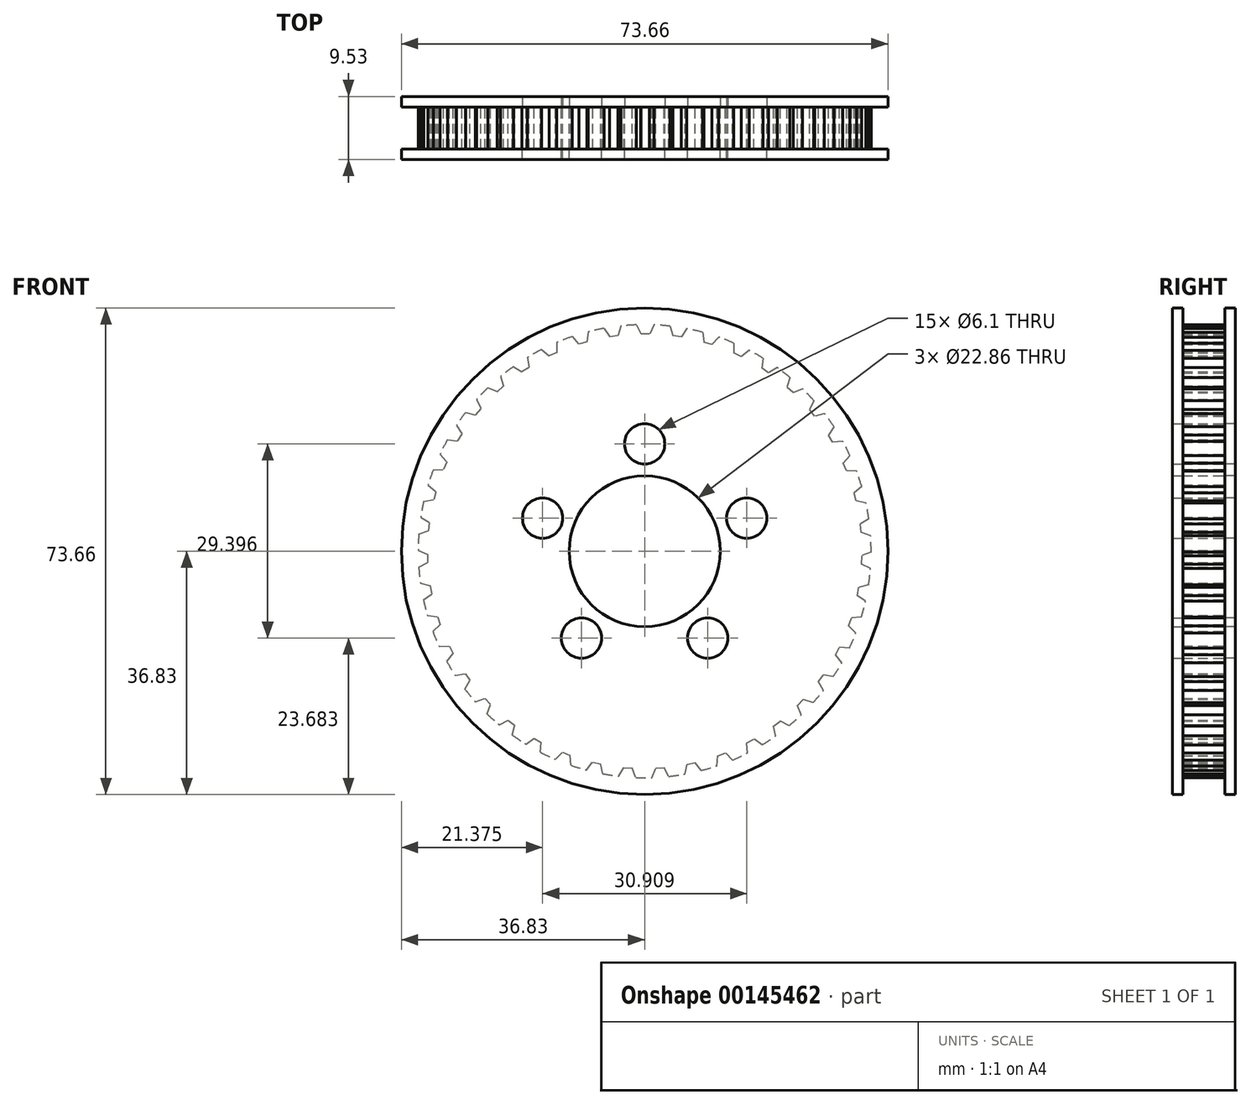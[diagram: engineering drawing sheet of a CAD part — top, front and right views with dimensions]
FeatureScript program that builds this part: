
annotation { "Feature Type Name" : "Feature", "Feature Type Description" : "" }
export const myFeature = defineFeature(function(context is Context, id is Id, definition is map)
    precondition{}
    {
        {
            var Q0;
            Q0=qCreatedBy(makeId("Front.planeOp"),FACE);
            var sketch = newSketch(context, id + "F0", { "sketchPlane" : qUnion([Q0])});
            skCircle(sketch, "E0", {"center": v(0, 0) * mm, "radius": 34.3 * mm});
            skLineSegment(sketch, "E1", {"start": v(-1.27, 34.27) * mm, "end": v(-0.64, 33) * mm});
            skLineSegment(sketch, "E2", {"start": v(-0.64, 33) * mm, "end": v(0, 33) * mm});
            skLineSegment(sketch, "E3.MirrorCS", {"start": v(0.64, 33) * mm, "end": v(0, 33) * mm});
            skLineSegment(sketch, "E4.MirrorCS", {"start": v(1.27, 34.27) * mm, "end": v(0.64, 33) * mm});
            skPoint(sketch, "E5", {"position": v(5.11, 33.9) * mm});
            skLineSegment(sketch, "E6", {"start": v(5.11, 33.9) * mm, "end": v(0, 0) * mm, "construction": true});
            skLineSegment(sketch, "E7", {"start": v(3.85, 34.07) * mm, "end": v(4.27, 32.61) * mm});
            skLineSegment(sketch, "E8", {"start": v(4.27, 32.61) * mm, "end": v(4.9, 32.52) * mm});
            skLineSegment(sketch, "E9.MirrorCS", {"start": v(5.53, 32.42) * mm, "end": v(4.9, 32.52) * mm});
            skLineSegment(sketch, "E10.MirrorCS", {"start": v(6.36, 33.7) * mm, "end": v(5.53, 32.42) * mm});
            skLineSegment(sketch, "E11.1.0", {"start": v(-31.43, -13.7) * mm, "end": v(-30.38, -12.6) * mm});
            skLineSegment(sketch, "E11.1.1", {"start": v(-32.36, -11.34) * mm, "end": v(-30.85, -11.42) * mm});
            skLineSegment(sketch, "E11.2.0", {"start": v(27.58, -20.37) * mm, "end": v(26.1, -20) * mm});
            skLineSegment(sketch, "E11.2.1", {"start": v(26, -22.36) * mm, "end": v(25.32, -21) * mm});
            skLineSegment(sketch, "E12.1.0", {"start": v(-0.52, 32.89) * mm, "end": v(0.11, 32.89) * mm});
            skLineSegment(sketch, "E12.1.1", {"start": v(0.75, 32.88) * mm, "end": v(0.11, 32.89) * mm});
            skLineSegment(sketch, "E12.1.2", {"start": v(-1.15, 34.27) * mm, "end": v(-0.52, 32.89) * mm});
            skLineSegment(sketch, "E12.1.3", {"start": v(1.39, 34.26) * mm, "end": v(0.75, 32.88) * mm});
            skLineSegment(sketch, "E12.2.0", {"start": v(-5.3, 32.46) * mm, "end": v(-4.68, 32.55) * mm});
            skLineSegment(sketch, "E12.2.1", {"start": v(-4.05, 32.64) * mm, "end": v(-4.68, 32.55) * mm});
            skLineSegment(sketch, "E12.2.2", {"start": v(-6.13, 33.74) * mm, "end": v(-5.3, 32.46) * mm});
            skLineSegment(sketch, "E12.2.3", {"start": v(-3.61, 34.1) * mm, "end": v(-4.05, 32.64) * mm});
            skLineSegment(sketch, "E12.3.0", {"start": v(-9.97, 31.34) * mm, "end": v(-9.36, 31.52) * mm});
            skLineSegment(sketch, "E12.3.1", {"start": v(-8.76, 31.7) * mm, "end": v(-9.36, 31.52) * mm});
            skLineSegment(sketch, "E12.3.2", {"start": v(-10.98, 32.49) * mm, "end": v(-9.97, 31.34) * mm});
            skLineSegment(sketch, "E12.3.3", {"start": v(-8.54, 33.2) * mm, "end": v(-8.76, 31.7) * mm});
            skLineSegment(sketch, "E12.4.0", {"start": v(-14.43, 29.56) * mm, "end": v(-13.86, 29.83) * mm});
            skLineSegment(sketch, "E12.4.1", {"start": v(-13.28, 30.1) * mm, "end": v(-13.86, 29.83) * mm});
            skLineSegment(sketch, "E12.4.2", {"start": v(-15.59, 30.54) * mm, "end": v(-14.43, 29.56) * mm});
            skLineSegment(sketch, "E12.4.3", {"start": v(-13.29, 31.61) * mm, "end": v(-13.28, 30.1) * mm});
            skLineSegment(sketch, "E12.5.0", {"start": v(-18.58, 27.14) * mm, "end": v(-18.05, 27.5) * mm});
            skLineSegment(sketch, "E12.5.1", {"start": v(-17.52, 27.84) * mm, "end": v(-18.05, 27.5) * mm});
            skLineSegment(sketch, "E12.5.2", {"start": v(-19.87, 27.95) * mm, "end": v(-18.58, 27.14) * mm});
            skLineSegment(sketch, "E12.5.3", {"start": v(-17.75, 29.34) * mm, "end": v(-17.52, 27.84) * mm});
            skLineSegment(sketch, "E12.6.0", {"start": v(-22.33, 24.15) * mm, "end": v(-21.86, 24.57) * mm});
            skLineSegment(sketch, "E12.6.1", {"start": v(-21.39, 25) * mm, "end": v(-21.86, 24.57) * mm});
            skLineSegment(sketch, "E12.6.2", {"start": v(-23.73, 24.76) * mm, "end": v(-22.33, 24.15) * mm});
            skLineSegment(sketch, "E12.6.3", {"start": v(-21.83, 26.44) * mm, "end": v(-21.39, 25) * mm});
            skLineSegment(sketch, "E12.7.0", {"start": v(-25.61, 20.64) * mm, "end": v(-25.2, 21.12) * mm});
            skLineSegment(sketch, "E12.7.1", {"start": v(-24.8, 21.61) * mm, "end": v(-25.2, 21.12) * mm});
            skLineSegment(sketch, "E12.7.2", {"start": v(-27.08, 21.04) * mm, "end": v(-25.61, 20.64) * mm});
            skLineSegment(sketch, "E12.7.3", {"start": v(-25.45, 22.98) * mm, "end": v(-24.8, 21.61) * mm});
            skLineSegment(sketch, "E12.8.0", {"start": v(-28.34, 16.69) * mm, "end": v(-28.01, 17.23) * mm});
            skLineSegment(sketch, "E12.8.1", {"start": v(-27.68, 17.77) * mm, "end": v(-28.01, 17.23) * mm});
            skLineSegment(sketch, "E12.8.2", {"start": v(-29.85, 16.87) * mm, "end": v(-28.34, 16.69) * mm});
            skLineSegment(sketch, "E12.8.3", {"start": v(-28.52, 19.03) * mm, "end": v(-27.68, 17.77) * mm});
            skLineSegment(sketch, "E12.9.0", {"start": v(-30.47, 12.38) * mm, "end": v(-30.22, 12.97) * mm});
            skLineSegment(sketch, "E12.9.1", {"start": v(-29.97, 13.55) * mm, "end": v(-30.22, 12.97) * mm});
            skLineSegment(sketch, "E12.9.2", {"start": v(-32, 12.34) * mm, "end": v(-30.47, 12.38) * mm});
            skLineSegment(sketch, "E12.9.3", {"start": v(-30.99, 14.68) * mm, "end": v(-29.97, 13.55) * mm});
            skLineSegment(sketch, "E12.10.0", {"start": v(-31.95, 7.81) * mm, "end": v(-31.79, 8.43) * mm});
            skLineSegment(sketch, "E12.10.1", {"start": v(-31.63, 9.04) * mm, "end": v(-31.79, 8.43) * mm});
            skLineSegment(sketch, "E12.10.2", {"start": v(-33.45, 7.56) * mm, "end": v(-31.95, 7.81) * mm});
            skLineSegment(sketch, "E12.10.3", {"start": v(-32.8, 10) * mm, "end": v(-31.63, 9.04) * mm});
            skLineSegment(sketch, "E12.11.0", {"start": v(-32.75, 3.08) * mm, "end": v(-32.68, 3.71) * mm});
            skLineSegment(sketch, "E12.11.1", {"start": v(-32.6, 4.34) * mm, "end": v(-32.68, 3.71) * mm});
            skLineSegment(sketch, "E12.11.2", {"start": v(-34.2, 2.6) * mm, "end": v(-32.75, 3.08) * mm});
            skLineSegment(sketch, "E12.11.3", {"start": v(-33.9, 5.13) * mm, "end": v(-32.6, 4.34) * mm});
            skLineSegment(sketch, "E12.12.0", {"start": v(-32.85, -1.72) * mm, "end": v(-32.87, -1.09) * mm});
            skLineSegment(sketch, "E12.12.1", {"start": v(-32.89, -0.45) * mm, "end": v(-32.87, -1.09) * mm});
            skLineSegment(sketch, "E12.12.2", {"start": v(-34.2, -2.4) * mm, "end": v(-32.85, -1.72) * mm});
            skLineSegment(sketch, "E12.12.3", {"start": v(-34.29, 0.14) * mm, "end": v(-32.89, -0.45) * mm});
            skLineSegment(sketch, "E12.13.0", {"start": v(-32.25, -6.49) * mm, "end": v(-32.36, -5.86) * mm});
            skLineSegment(sketch, "E12.13.1", {"start": v(-32.47, -5.24) * mm, "end": v(-32.36, -5.86) * mm});
            skLineSegment(sketch, "E12.13.2", {"start": v(-33.5, -7.36) * mm, "end": v(-32.25, -6.49) * mm});
            skLineSegment(sketch, "E12.13.3", {"start": v(-33.94, -4.86) * mm, "end": v(-32.47, -5.24) * mm});
            skLineSegment(sketch, "E12.14.0", {"start": v(-30.96, -11.11) * mm, "end": v(-31.16, -10.51) * mm});
            skLineSegment(sketch, "E12.14.1", {"start": v(-31.36, -9.9) * mm, "end": v(-31.16, -10.51) * mm});
            skLineSegment(sketch, "E12.14.2", {"start": v(-32.06, -12.15) * mm, "end": v(-30.96, -11.11) * mm});
            skLineSegment(sketch, "E12.14.3", {"start": v(-32.88, -9.75) * mm, "end": v(-31.36, -9.9) * mm});
            skLineSegment(sketch, "E12.15.0", {"start": v(-29.01, -15.5) * mm, "end": v(-29.3, -14.94) * mm});
            skLineSegment(sketch, "E12.15.1", {"start": v(-29.59, -14.37) * mm, "end": v(-29.3, -14.94) * mm});
            skLineSegment(sketch, "E12.15.2", {"start": v(-29.95, -16.7) * mm, "end": v(-29.01, -15.5) * mm});
            skLineSegment(sketch, "E12.15.3", {"start": v(-31.1, -14.43) * mm, "end": v(-29.59, -14.37) * mm});
            skLineSegment(sketch, "E12.16.0", {"start": v(-26.44, -19.56) * mm, "end": v(-26.81, -19.04) * mm});
            skLineSegment(sketch, "E12.16.1", {"start": v(-27.18, -18.52) * mm, "end": v(-26.81, -19.04) * mm});
            skLineSegment(sketch, "E12.16.2", {"start": v(-27.2, -20.88) * mm, "end": v(-26.44, -19.56) * mm});
            skLineSegment(sketch, "E12.16.3", {"start": v(-28.67, -18.8) * mm, "end": v(-27.18, -18.52) * mm});
            skLineSegment(sketch, "E12.17.0", {"start": v(-23.32, -23.2) * mm, "end": v(-23.75, -22.74) * mm});
            skLineSegment(sketch, "E12.17.1", {"start": v(-24.2, -22.28) * mm, "end": v(-23.75, -22.74) * mm});
            skLineSegment(sketch, "E12.17.2", {"start": v(-23.87, -24.61) * mm, "end": v(-23.32, -23.2) * mm});
            skLineSegment(sketch, "E12.17.3", {"start": v(-25.63, -22.78) * mm, "end": v(-24.2, -22.28) * mm});
            skLineSegment(sketch, "E12.18.0", {"start": v(-19.69, -26.35) * mm, "end": v(-20.19, -25.96) * mm});
            skLineSegment(sketch, "E12.18.1", {"start": v(-20.7, -25.57) * mm, "end": v(-20.19, -25.96) * mm});
            skLineSegment(sketch, "E12.18.2", {"start": v(-20.03, -27.83) * mm, "end": v(-19.69, -26.35) * mm});
            skLineSegment(sketch, "E12.18.3", {"start": v(-22.04, -26.27) * mm, "end": v(-20.7, -25.57) * mm});
            skLineSegment(sketch, "E12.19.0", {"start": v(-15.64, -28.94) * mm, "end": v(-16.2, -28.62) * mm});
            skLineSegment(sketch, "E12.19.1", {"start": v(-16.75, -28.3) * mm, "end": v(-16.2, -28.62) * mm});
            skLineSegment(sketch, "E12.19.2", {"start": v(-15.77, -30.45) * mm, "end": v(-15.64, -28.94) * mm});
            skLineSegment(sketch, "E12.19.3", {"start": v(-17.98, -29.2) * mm, "end": v(-16.75, -28.3) * mm});
            skLineSegment(sketch, "E12.20.0", {"start": v(-11.26, -30.9) * mm, "end": v(-11.85, -30.68) * mm});
            skLineSegment(sketch, "E12.20.1", {"start": v(-12.45, -30.45) * mm, "end": v(-11.85, -30.68) * mm});
            skLineSegment(sketch, "E12.20.2", {"start": v(-11.17, -32.42) * mm, "end": v(-11.26, -30.9) * mm});
            skLineSegment(sketch, "E12.20.3", {"start": v(-13.54, -31.5) * mm, "end": v(-12.45, -30.45) * mm});
            skLineSegment(sketch, "E12.21.0", {"start": v(-6.64, -32.21) * mm, "end": v(-7.26, -32.07) * mm});
            skLineSegment(sketch, "E12.21.1", {"start": v(-7.88, -31.93) * mm, "end": v(-7.26, -32.07) * mm});
            skLineSegment(sketch, "E12.21.2", {"start": v(-6.33, -33.7) * mm, "end": v(-6.64, -32.21) * mm});
            skLineSegment(sketch, "E12.21.3", {"start": v(-8.8, -33.14) * mm, "end": v(-7.88, -31.93) * mm});
            skLineSegment(sketch, "E12.22.0", {"start": v(-1.88, -32.84) * mm, "end": v(-2.51, -32.8) * mm});
            skLineSegment(sketch, "E12.22.1", {"start": v(-3.15, -32.74) * mm, "end": v(-2.51, -32.8) * mm});
            skLineSegment(sketch, "E12.22.2", {"start": v(-1.35, -34.26) * mm, "end": v(-1.88, -32.84) * mm});
            skLineSegment(sketch, "E12.22.3", {"start": v(-3.89, -34.07) * mm, "end": v(-3.15, -32.74) * mm});
            skLineSegment(sketch, "E12.23.0", {"start": v(2.92, -32.76) * mm, "end": v(2.29, -32.8) * mm});
            skLineSegment(sketch, "E12.23.1", {"start": v(1.65, -32.85) * mm, "end": v(2.29, -32.8) * mm});
            skLineSegment(sketch, "E12.23.2", {"start": v(3.65, -34.1) * mm, "end": v(2.92, -32.76) * mm});
            skLineSegment(sketch, "E12.23.3", {"start": v(1.12, -34.27) * mm, "end": v(1.65, -32.85) * mm});
            skLineSegment(sketch, "E12.24.0", {"start": v(7.66, -31.99) * mm, "end": v(7.04, -32.12) * mm});
            skLineSegment(sketch, "E12.24.1", {"start": v(6.42, -32.26) * mm, "end": v(7.04, -32.12) * mm});
            skLineSegment(sketch, "E12.24.2", {"start": v(8.57, -33.2) * mm, "end": v(7.66, -31.99) * mm});
            skLineSegment(sketch, "E12.24.3", {"start": v(6.1, -33.74) * mm, "end": v(6.42, -32.26) * mm});
            skLineSegment(sketch, "E12.25.0", {"start": v(12.24, -30.53) * mm, "end": v(11.64, -30.76) * mm});
            skLineSegment(sketch, "E12.25.1", {"start": v(11.05, -30.98) * mm, "end": v(11.64, -30.76) * mm});
            skLineSegment(sketch, "E12.25.2", {"start": v(13.32, -31.6) * mm, "end": v(12.24, -30.53) * mm});
            skLineSegment(sketch, "E12.25.3", {"start": v(10.94, -32.5) * mm, "end": v(11.05, -30.98) * mm});
            skLineSegment(sketch, "E12.26.0", {"start": v(16.55, -28.43) * mm, "end": v(16, -28.73) * mm});
            skLineSegment(sketch, "E12.26.1", {"start": v(15.44, -29.04) * mm, "end": v(16, -28.73) * mm});
            skLineSegment(sketch, "E12.26.2", {"start": v(17.78, -29.32) * mm, "end": v(16.55, -28.43) * mm});
            skLineSegment(sketch, "E12.26.3", {"start": v(15.56, -30.56) * mm, "end": v(15.44, -29.04) * mm});
            skLineSegment(sketch, "E12.27.0", {"start": v(20.51, -25.71) * mm, "end": v(20, -26.1) * mm});
            skLineSegment(sketch, "E12.27.1", {"start": v(19.5, -26.49) * mm, "end": v(20, -26.1) * mm});
            skLineSegment(sketch, "E12.27.2", {"start": v(21.86, -26.42) * mm, "end": v(20.51, -25.71) * mm});
            skLineSegment(sketch, "E12.27.3", {"start": v(19.84, -27.97) * mm, "end": v(19.5, -26.49) * mm});
            skLineSegment(sketch, "E12.28.0", {"start": v(24.04, -22.45) * mm, "end": v(23.6, -22.9) * mm});
            skLineSegment(sketch, "E12.28.1", {"start": v(23.15, -23.36) * mm, "end": v(23.6, -22.9) * mm});
            skLineSegment(sketch, "E12.28.2", {"start": v(25.47, -22.96) * mm, "end": v(24.04, -22.45) * mm});
            skLineSegment(sketch, "E12.28.3", {"start": v(23.7, -24.78) * mm, "end": v(23.15, -23.36) * mm});
            skLineSegment(sketch, "E12.29.0", {"start": v(27.05, -18.71) * mm, "end": v(26.68, -19.23) * mm});
            skLineSegment(sketch, "E12.29.1", {"start": v(26.3, -19.74) * mm, "end": v(26.68, -19.23) * mm});
            skLineSegment(sketch, "E12.29.2", {"start": v(28.54, -19) * mm, "end": v(27.05, -18.71) * mm});
            skLineSegment(sketch, "E12.29.3", {"start": v(27.06, -21.07) * mm, "end": v(26.3, -19.74) * mm});
            skLineSegment(sketch, "E12.30.0", {"start": v(29.49, -14.58) * mm, "end": v(29.2, -15.14) * mm});
            skLineSegment(sketch, "E12.30.1", {"start": v(28.9, -15.7) * mm, "end": v(29.2, -15.14) * mm});
            skLineSegment(sketch, "E12.30.2", {"start": v(31, -14.65) * mm, "end": v(29.49, -14.58) * mm});
            skLineSegment(sketch, "E12.30.3", {"start": v(29.84, -16.9) * mm, "end": v(28.9, -15.7) * mm});
            skLineSegment(sketch, "E12.31.0", {"start": v(31.3, -10.13) * mm, "end": v(31.09, -10.73) * mm});
            skLineSegment(sketch, "E12.31.1", {"start": v(30.88, -11.33) * mm, "end": v(31.09, -10.73) * mm});
            skLineSegment(sketch, "E12.31.2", {"start": v(32.8, -9.98) * mm, "end": v(31.3, -10.13) * mm});
            skLineSegment(sketch, "E12.31.3", {"start": v(31.98, -12.38) * mm, "end": v(30.88, -11.33) * mm});
            skLineSegment(sketch, "E12.32.0", {"start": v(32.44, -5.46) * mm, "end": v(32.32, -6.09) * mm});
            skLineSegment(sketch, "E12.32.1", {"start": v(32.2, -6.7) * mm, "end": v(32.32, -6.09) * mm});
            skLineSegment(sketch, "E12.32.2", {"start": v(33.9, -5.1) * mm, "end": v(32.44, -5.46) * mm});
            skLineSegment(sketch, "E12.32.3", {"start": v(33.44, -7.59) * mm, "end": v(32.2, -6.7) * mm});
            skLineSegment(sketch, "E12.33.0", {"start": v(32.89, -0.68) * mm, "end": v(32.86, -1.32) * mm});
            skLineSegment(sketch, "E12.33.1", {"start": v(32.83, -1.95) * mm, "end": v(32.86, -1.32) * mm});
            skLineSegment(sketch, "E12.33.2", {"start": v(34.29, -0.1) * mm, "end": v(32.89, -0.68) * mm});
            skLineSegment(sketch, "E12.33.3", {"start": v(34.19, -2.64) * mm, "end": v(32.83, -1.95) * mm});
            skLineSegment(sketch, "E12.34.0", {"start": v(32.63, 4.11) * mm, "end": v(32.7, 3.48) * mm});
            skLineSegment(sketch, "E12.34.1", {"start": v(32.77, 2.85) * mm, "end": v(32.7, 3.48) * mm});
            skLineSegment(sketch, "E12.34.2", {"start": v(33.94, 4.9) * mm, "end": v(32.63, 4.11) * mm});
            skLineSegment(sketch, "E12.34.3", {"start": v(34.2, 2.37) * mm, "end": v(32.77, 2.85) * mm});
            skLineSegment(sketch, "E12.35.0", {"start": v(31.69, 8.82) * mm, "end": v(31.85, 8.2) * mm});
            skLineSegment(sketch, "E12.35.1", {"start": v(32, 7.6) * mm, "end": v(31.85, 8.2) * mm});
            skLineSegment(sketch, "E12.35.2", {"start": v(32.87, 9.78) * mm, "end": v(31.69, 8.82) * mm});
            skLineSegment(sketch, "E12.35.3", {"start": v(33.5, 7.32) * mm, "end": v(32, 7.6) * mm});
            skLineSegment(sketch, "E12.36.0", {"start": v(30.07, 13.34) * mm, "end": v(30.31, 12.76) * mm});
            skLineSegment(sketch, "E12.36.1", {"start": v(30.56, 12.17) * mm, "end": v(30.31, 12.76) * mm});
            skLineSegment(sketch, "E12.36.2", {"start": v(31.1, 14.46) * mm, "end": v(30.07, 13.34) * mm});
            skLineSegment(sketch, "E12.36.3", {"start": v(32.08, 12.12) * mm, "end": v(30.56, 12.17) * mm});
            skLineSegment(sketch, "E12.37.0", {"start": v(27.8, 17.58) * mm, "end": v(28.13, 17.03) * mm});
            skLineSegment(sketch, "E12.37.1", {"start": v(28.46, 16.5) * mm, "end": v(28.13, 17.03) * mm});
            skLineSegment(sketch, "E12.37.2", {"start": v(28.65, 18.84) * mm, "end": v(27.8, 17.58) * mm});
            skLineSegment(sketch, "E12.37.3", {"start": v(29.97, 16.66) * mm, "end": v(28.46, 16.5) * mm});
            skLineSegment(sketch, "E12.38.0", {"start": v(24.95, 21.44) * mm, "end": v(25.35, 20.95) * mm});
            skLineSegment(sketch, "E12.38.1", {"start": v(25.76, 20.46) * mm, "end": v(25.35, 20.95) * mm});
            skLineSegment(sketch, "E12.38.2", {"start": v(25.6, 22.8) * mm, "end": v(24.95, 21.44) * mm});
            skLineSegment(sketch, "E12.38.3", {"start": v(27.22, 20.85) * mm, "end": v(25.76, 20.46) * mm});
            skLineSegment(sketch, "E12.39.0", {"start": v(21.56, 24.84) * mm, "end": v(22.03, 24.42) * mm});
            skLineSegment(sketch, "E12.39.1", {"start": v(22.5, 24) * mm, "end": v(22.03, 24.42) * mm});
            skLineSegment(sketch, "E12.39.2", {"start": v(22.01, 26.3) * mm, "end": v(21.56, 24.84) * mm});
            skLineSegment(sketch, "E12.39.3", {"start": v(23.9, 24.6) * mm, "end": v(22.5, 24) * mm});
            skCircle(sketch, "E13", {"center": v(0, 16.25) * mm, "radius": 3.05 * mm});
            skCircle(sketch, "E14.1.0", {"center": v(-15.45, 5.02) * mm, "radius": 3.05 * mm});
            skCircle(sketch, "E14.2.0", {"center": v(-9.55, -13.15) * mm, "radius": 3.05 * mm});
            skCircle(sketch, "E14.3.0", {"center": v(9.55, -13.15) * mm, "radius": 3.05 * mm});
            skCircle(sketch, "E14.4.0", {"center": v(15.45, 5.02) * mm, "radius": 3.05 * mm});
            skLineSegment(sketch, "E15.1.40.0", {"start": v(17.71, 27.72) * mm, "end": v(18.24, 27.36) * mm});
            skLineSegment(sketch, "E15.3.40.0", {"start": v(18.77, 27.01) * mm, "end": v(18.24, 27.36) * mm});
            skLineSegment(sketch, "E15.6.40.0", {"start": v(17.95, 29.22) * mm, "end": v(17.71, 27.72) * mm});
            skLineSegment(sketch, "E15.9.40.0", {"start": v(20.06, 27.8) * mm, "end": v(18.77, 27.01) * mm});
            skLineSegment(sketch, "E16.1.41.0", {"start": v(13.49, 30) * mm, "end": v(14.06, 29.73) * mm});
            skLineSegment(sketch, "E16.3.41.0", {"start": v(14.64, 29.46) * mm, "end": v(14.06, 29.73) * mm});
            skLineSegment(sketch, "E16.6.41.0", {"start": v(13.5, 31.52) * mm, "end": v(13.49, 30) * mm});
            skLineSegment(sketch, "E16.9.41.0", {"start": v(15.8, 30.43) * mm, "end": v(14.64, 29.46) * mm});
            skLineSegment(sketch, "E17.1.42.0", {"start": v(8.98, 31.64) * mm, "end": v(9.58, 31.46) * mm});
            skLineSegment(sketch, "E17.3.42.0", {"start": v(10.2, 31.27) * mm, "end": v(9.58, 31.46) * mm});
            skLineSegment(sketch, "E17.6.42.0", {"start": v(8.77, 33.15) * mm, "end": v(8.98, 31.64) * mm});
            skLineSegment(sketch, "E17.9.42.0", {"start": v(11.2, 32.4) * mm, "end": v(10.2, 31.27) * mm});
            skCircle(sketch, "E18", {"center": v(0, 0) * mm, "radius": 11.43 * mm});
            skLineSegment(sketch, "E19", {"start": v(-8.54, 33.2) * mm, "end": v(-6.13, 33.74) * mm, "construction": true});
            skSolve(sketch);
        }
        {
            var Q0;
            {var subQ60=sQuery(id+"F0.wireOp",EDGE,"E7");Q0=makeQuery(id+"F0.imprint","IMPRINT",FACE,{"disambiguationData":[TD([[makeQuery(id+"F0.imprint","IMPRINT",EDGE,{"derivedFrom":subQ60}),-1.0]])]});}
            extrude(context, id + "F1", {"entities" : qUnion([Q0]), "depth" : 6.35 * mm});
        }
        {
            var Q0;
            Q0=makeQuery(id+"F1.opExtrude","CAP_FACE",FACE,{"disambiguationData":[OSD([sQuery(id+"F0.wireOp",EDGE,"E0"),sQuery(id+"F0.wireOp",EDGE,"E1"),sQuery(id+"F0.wireOp",EDGE,"E4.MirrorCS"),sQuery(id+"F0.wireOp",EDGE,"E7"),sQuery(id+"F0.wireOp",EDGE,"E8"),sQuery(id+"F0.wireOp",EDGE,"E9.MirrorCS"),sQuery(id+"F0.wireOp",EDGE,"E10.MirrorCS"),sQuery(id+"F0.wireOp",EDGE,"E12.1.0"),sQuery(id+"F0.wireOp",EDGE,"E12.1.1"),sQuery(id+"F0.wireOp",EDGE,"E12.1.2"),sQuery(id+"F0.wireOp",EDGE,"E12.1.3"),sQuery(id+"F0.wireOp",EDGE,"E12.2.0"),sQuery(id+"F0.wireOp",EDGE,"E12.2.1"),sQuery(id+"F0.wireOp",EDGE,"E12.2.2"),sQuery(id+"F0.wireOp",EDGE,"E12.2.3"),sQuery(id+"F0.wireOp",EDGE,"E12.3.0"),sQuery(id+"F0.wireOp",EDGE,"E12.3.1"),sQuery(id+"F0.wireOp",EDGE,"E12.3.2"),sQuery(id+"F0.wireOp",EDGE,"E12.3.3"),sQuery(id+"F0.wireOp",EDGE,"E12.4.0"),sQuery(id+"F0.wireOp",EDGE,"E12.4.1"),sQuery(id+"F0.wireOp",EDGE,"E12.4.2"),sQuery(id+"F0.wireOp",EDGE,"E12.4.3"),sQuery(id+"F0.wireOp",EDGE,"E12.5.0"),sQuery(id+"F0.wireOp",EDGE,"E12.5.1"),sQuery(id+"F0.wireOp",EDGE,"E12.5.2"),sQuery(id+"F0.wireOp",EDGE,"E12.5.3"),sQuery(id+"F0.wireOp",EDGE,"E12.6.0"),sQuery(id+"F0.wireOp",EDGE,"E12.6.1"),sQuery(id+"F0.wireOp",EDGE,"E12.6.2"),sQuery(id+"F0.wireOp",EDGE,"E12.6.3"),sQuery(id+"F0.wireOp",EDGE,"E12.7.0"),sQuery(id+"F0.wireOp",EDGE,"E12.7.1"),sQuery(id+"F0.wireOp",EDGE,"E12.7.2"),sQuery(id+"F0.wireOp",EDGE,"E12.7.3"),sQuery(id+"F0.wireOp",EDGE,"E12.8.0"),sQuery(id+"F0.wireOp",EDGE,"E12.8.1"),sQuery(id+"F0.wireOp",EDGE,"E12.8.2"),sQuery(id+"F0.wireOp",EDGE,"E12.8.3"),sQuery(id+"F0.wireOp",EDGE,"E12.9.0"),sQuery(id+"F0.wireOp",EDGE,"E12.9.1"),sQuery(id+"F0.wireOp",EDGE,"E12.9.2"),sQuery(id+"F0.wireOp",EDGE,"E12.9.3"),sQuery(id+"F0.wireOp",EDGE,"E12.10.0"),sQuery(id+"F0.wireOp",EDGE,"E12.10.1"),sQuery(id+"F0.wireOp",EDGE,"E12.10.2"),sQuery(id+"F0.wireOp",EDGE,"E12.10.3"),sQuery(id+"F0.wireOp",EDGE,"E12.11.0"),sQuery(id+"F0.wireOp",EDGE,"E12.11.1"),sQuery(id+"F0.wireOp",EDGE,"E12.11.2"),sQuery(id+"F0.wireOp",EDGE,"E12.11.3"),sQuery(id+"F0.wireOp",EDGE,"E12.12.0"),sQuery(id+"F0.wireOp",EDGE,"E12.12.1"),sQuery(id+"F0.wireOp",EDGE,"E12.12.2"),sQuery(id+"F0.wireOp",EDGE,"E12.12.3"),sQuery(id+"F0.wireOp",EDGE,"E12.13.0"),sQuery(id+"F0.wireOp",EDGE,"E12.13.1"),sQuery(id+"F0.wireOp",EDGE,"E12.13.2"),sQuery(id+"F0.wireOp",EDGE,"E12.13.3"),sQuery(id+"F0.wireOp",EDGE,"E12.14.0"),sQuery(id+"F0.wireOp",EDGE,"E12.14.1"),sQuery(id+"F0.wireOp",EDGE,"E12.14.2"),sQuery(id+"F0.wireOp",EDGE,"E12.14.3"),sQuery(id+"F0.wireOp",EDGE,"E12.15.0"),sQuery(id+"F0.wireOp",EDGE,"E12.15.1"),sQuery(id+"F0.wireOp",EDGE,"E12.15.2"),sQuery(id+"F0.wireOp",EDGE,"E12.15.3"),sQuery(id+"F0.wireOp",EDGE,"E12.16.0"),sQuery(id+"F0.wireOp",EDGE,"E12.16.1"),sQuery(id+"F0.wireOp",EDGE,"E12.16.2"),sQuery(id+"F0.wireOp",EDGE,"E12.16.3"),sQuery(id+"F0.wireOp",EDGE,"E12.17.0"),sQuery(id+"F0.wireOp",EDGE,"E12.17.1"),sQuery(id+"F0.wireOp",EDGE,"E12.17.2"),sQuery(id+"F0.wireOp",EDGE,"E12.17.3"),sQuery(id+"F0.wireOp",EDGE,"E12.18.0"),sQuery(id+"F0.wireOp",EDGE,"E12.18.1"),sQuery(id+"F0.wireOp",EDGE,"E12.18.2"),sQuery(id+"F0.wireOp",EDGE,"E12.18.3"),sQuery(id+"F0.wireOp",EDGE,"E12.19.0"),sQuery(id+"F0.wireOp",EDGE,"E12.19.1"),sQuery(id+"F0.wireOp",EDGE,"E12.19.2"),sQuery(id+"F0.wireOp",EDGE,"E12.19.3"),sQuery(id+"F0.wireOp",EDGE,"E12.20.0"),sQuery(id+"F0.wireOp",EDGE,"E12.20.1"),sQuery(id+"F0.wireOp",EDGE,"E12.20.2"),sQuery(id+"F0.wireOp",EDGE,"E12.20.3"),sQuery(id+"F0.wireOp",EDGE,"E12.21.0"),sQuery(id+"F0.wireOp",EDGE,"E12.21.1"),sQuery(id+"F0.wireOp",EDGE,"E12.21.2"),sQuery(id+"F0.wireOp",EDGE,"E12.21.3"),sQuery(id+"F0.wireOp",EDGE,"E12.22.0"),sQuery(id+"F0.wireOp",EDGE,"E12.22.1"),sQuery(id+"F0.wireOp",EDGE,"E12.22.2"),sQuery(id+"F0.wireOp",EDGE,"E12.22.3"),sQuery(id+"F0.wireOp",EDGE,"E12.23.0"),sQuery(id+"F0.wireOp",EDGE,"E12.23.1"),sQuery(id+"F0.wireOp",EDGE,"E12.23.2"),sQuery(id+"F0.wireOp",EDGE,"E12.23.3"),sQuery(id+"F0.wireOp",EDGE,"E12.24.0"),sQuery(id+"F0.wireOp",EDGE,"E12.24.1"),sQuery(id+"F0.wireOp",EDGE,"E12.24.2"),sQuery(id+"F0.wireOp",EDGE,"E12.24.3"),sQuery(id+"F0.wireOp",EDGE,"E12.25.0"),sQuery(id+"F0.wireOp",EDGE,"E12.25.1"),sQuery(id+"F0.wireOp",EDGE,"E12.25.2"),sQuery(id+"F0.wireOp",EDGE,"E12.25.3"),sQuery(id+"F0.wireOp",EDGE,"E12.26.0"),sQuery(id+"F0.wireOp",EDGE,"E12.26.1"),sQuery(id+"F0.wireOp",EDGE,"E12.26.2"),sQuery(id+"F0.wireOp",EDGE,"E12.26.3"),sQuery(id+"F0.wireOp",EDGE,"E12.27.0"),sQuery(id+"F0.wireOp",EDGE,"E12.27.1"),sQuery(id+"F0.wireOp",EDGE,"E12.27.2"),sQuery(id+"F0.wireOp",EDGE,"E12.27.3"),sQuery(id+"F0.wireOp",EDGE,"E12.28.0"),sQuery(id+"F0.wireOp",EDGE,"E12.28.1"),sQuery(id+"F0.wireOp",EDGE,"E12.28.2"),sQuery(id+"F0.wireOp",EDGE,"E12.28.3"),sQuery(id+"F0.wireOp",EDGE,"E12.29.0"),sQuery(id+"F0.wireOp",EDGE,"E12.29.1"),sQuery(id+"F0.wireOp",EDGE,"E12.29.2"),sQuery(id+"F0.wireOp",EDGE,"E12.29.3"),sQuery(id+"F0.wireOp",EDGE,"E12.30.0"),sQuery(id+"F0.wireOp",EDGE,"E12.30.1"),sQuery(id+"F0.wireOp",EDGE,"E12.30.2"),sQuery(id+"F0.wireOp",EDGE,"E12.30.3"),sQuery(id+"F0.wireOp",EDGE,"E12.31.0"),sQuery(id+"F0.wireOp",EDGE,"E12.31.1"),sQuery(id+"F0.wireOp",EDGE,"E12.31.2"),sQuery(id+"F0.wireOp",EDGE,"E12.31.3"),sQuery(id+"F0.wireOp",EDGE,"E12.32.0"),sQuery(id+"F0.wireOp",EDGE,"E12.32.1"),sQuery(id+"F0.wireOp",EDGE,"E12.32.2"),sQuery(id+"F0.wireOp",EDGE,"E12.32.3"),sQuery(id+"F0.wireOp",EDGE,"E12.33.0"),sQuery(id+"F0.wireOp",EDGE,"E12.33.1"),sQuery(id+"F0.wireOp",EDGE,"E12.33.2"),sQuery(id+"F0.wireOp",EDGE,"E12.33.3"),sQuery(id+"F0.wireOp",EDGE,"E12.34.0"),sQuery(id+"F0.wireOp",EDGE,"E12.34.1"),sQuery(id+"F0.wireOp",EDGE,"E12.34.2"),sQuery(id+"F0.wireOp",EDGE,"E12.34.3"),sQuery(id+"F0.wireOp",EDGE,"E12.35.0"),sQuery(id+"F0.wireOp",EDGE,"E12.35.1"),sQuery(id+"F0.wireOp",EDGE,"E12.35.2"),sQuery(id+"F0.wireOp",EDGE,"E12.35.3"),sQuery(id+"F0.wireOp",EDGE,"E12.36.0"),sQuery(id+"F0.wireOp",EDGE,"E12.36.1"),sQuery(id+"F0.wireOp",EDGE,"E12.36.2"),sQuery(id+"F0.wireOp",EDGE,"E12.36.3"),sQuery(id+"F0.wireOp",EDGE,"E12.37.0"),sQuery(id+"F0.wireOp",EDGE,"E12.37.1"),sQuery(id+"F0.wireOp",EDGE,"E12.37.2"),sQuery(id+"F0.wireOp",EDGE,"E12.37.3"),sQuery(id+"F0.wireOp",EDGE,"E12.38.0"),sQuery(id+"F0.wireOp",EDGE,"E12.38.1"),sQuery(id+"F0.wireOp",EDGE,"E12.38.2"),sQuery(id+"F0.wireOp",EDGE,"E12.38.3"),sQuery(id+"F0.wireOp",EDGE,"E12.39.0"),sQuery(id+"F0.wireOp",EDGE,"E12.39.1"),sQuery(id+"F0.wireOp",EDGE,"E12.39.2"),sQuery(id+"F0.wireOp",EDGE,"E12.39.3"),sQuery(id+"F0.wireOp",EDGE,"E12.40.0"),sQuery(id+"F0.wireOp",EDGE,"E12.40.1"),sQuery(id+"F0.wireOp",EDGE,"E12.40.2"),sQuery(id+"F0.wireOp",EDGE,"E12.40.3"),sQuery(id+"F0.wireOp",EDGE,"E12.41.0"),sQuery(id+"F0.wireOp",EDGE,"E12.41.1"),sQuery(id+"F0.wireOp",EDGE,"E12.41.2"),sQuery(id+"F0.wireOp",EDGE,"E12.41.3"),sQuery(id+"F0.wireOp",EDGE,"E13"),sQuery(id+"F0.wireOp",EDGE,"E14.1.0"),sQuery(id+"F0.wireOp",EDGE,"E14.2.0"),sQuery(id+"F0.wireOp",EDGE,"E14.3.0"),sQuery(id+"F0.wireOp",EDGE,"E14.4.0"),sQuery(id+"F0.wireOp",EDGE,"E14.5.0"),sQuery(id+"F0.wireOp",EDGE,"E14.6.0"),sQuery(id+"F0.wireOp",EDGE,"E14.7.0"),sQuery(id+"F0.wireOp",EDGE,"E14.8.0"),sQuery(id+"F0.wireOp",EDGE,"E14.9.0")])],"isStart":false});
            var sketch = newSketch(context, id + "F2", { "sketchPlane" : qUnion([Q0])});
            skCircle(sketch, "E20", {"center": v(0, 0) * mm, "radius": 36.83 * mm});
            skCircle(sketch, "E21", {"center": v(-15.45, 5.02) * mm, "radius": 3.05 * mm});
            skCircle(sketch, "E22", {"center": v(0, 16.25) * mm, "radius": 3.05 * mm});
            skCircle(sketch, "E23", {"center": v(15.45, 5.02) * mm, "radius": 3.05 * mm});
            skCircle(sketch, "E24", {"center": v(9.55, -13.15) * mm, "radius": 3.05 * mm});
            skCircle(sketch, "E25", {"center": v(-9.55, -13.15) * mm, "radius": 3.05 * mm});
            skCircle(sketch, "E26", {"center": v(0, 0) * mm, "radius": 11.43 * mm});
            skSolve(sketch);
        }
        {
            var Q0;
            Q0 = qSketchRegion(id + "F2", true);
            extrude(context, id + "F3", {"entities" : qUnion([Q0]), "depth" : 1.59 * mm});
        }
        {
            var Q0;
            Q0=makeQuery(id+"F1.opExtrude","CAP_FACE",FACE,{"disambiguationData":[OSD([sQuery(id+"F0.wireOp",EDGE,"E0"),sQuery(id+"F0.wireOp",EDGE,"E1"),sQuery(id+"F0.wireOp",EDGE,"E4.MirrorCS"),sQuery(id+"F0.wireOp",EDGE,"E7"),sQuery(id+"F0.wireOp",EDGE,"E8"),sQuery(id+"F0.wireOp",EDGE,"E9.MirrorCS"),sQuery(id+"F0.wireOp",EDGE,"E10.MirrorCS"),sQuery(id+"F0.wireOp",EDGE,"E12.1.0"),sQuery(id+"F0.wireOp",EDGE,"E12.1.1"),sQuery(id+"F0.wireOp",EDGE,"E12.1.2"),sQuery(id+"F0.wireOp",EDGE,"E12.1.3"),sQuery(id+"F0.wireOp",EDGE,"E12.2.0"),sQuery(id+"F0.wireOp",EDGE,"E12.2.1"),sQuery(id+"F0.wireOp",EDGE,"E12.2.2"),sQuery(id+"F0.wireOp",EDGE,"E12.2.3"),sQuery(id+"F0.wireOp",EDGE,"E12.3.0"),sQuery(id+"F0.wireOp",EDGE,"E12.3.1"),sQuery(id+"F0.wireOp",EDGE,"E12.3.2"),sQuery(id+"F0.wireOp",EDGE,"E12.3.3"),sQuery(id+"F0.wireOp",EDGE,"E12.4.0"),sQuery(id+"F0.wireOp",EDGE,"E12.4.1"),sQuery(id+"F0.wireOp",EDGE,"E12.4.2"),sQuery(id+"F0.wireOp",EDGE,"E12.4.3"),sQuery(id+"F0.wireOp",EDGE,"E12.5.0"),sQuery(id+"F0.wireOp",EDGE,"E12.5.1"),sQuery(id+"F0.wireOp",EDGE,"E12.5.2"),sQuery(id+"F0.wireOp",EDGE,"E12.5.3"),sQuery(id+"F0.wireOp",EDGE,"E12.6.0"),sQuery(id+"F0.wireOp",EDGE,"E12.6.1"),sQuery(id+"F0.wireOp",EDGE,"E12.6.2"),sQuery(id+"F0.wireOp",EDGE,"E12.6.3"),sQuery(id+"F0.wireOp",EDGE,"E12.7.0"),sQuery(id+"F0.wireOp",EDGE,"E12.7.1"),sQuery(id+"F0.wireOp",EDGE,"E12.7.2"),sQuery(id+"F0.wireOp",EDGE,"E12.7.3"),sQuery(id+"F0.wireOp",EDGE,"E12.8.0"),sQuery(id+"F0.wireOp",EDGE,"E12.8.1"),sQuery(id+"F0.wireOp",EDGE,"E12.8.2"),sQuery(id+"F0.wireOp",EDGE,"E12.8.3"),sQuery(id+"F0.wireOp",EDGE,"E12.9.0"),sQuery(id+"F0.wireOp",EDGE,"E12.9.1"),sQuery(id+"F0.wireOp",EDGE,"E12.9.2"),sQuery(id+"F0.wireOp",EDGE,"E12.9.3"),sQuery(id+"F0.wireOp",EDGE,"E12.10.0"),sQuery(id+"F0.wireOp",EDGE,"E12.10.1"),sQuery(id+"F0.wireOp",EDGE,"E12.10.2"),sQuery(id+"F0.wireOp",EDGE,"E12.10.3"),sQuery(id+"F0.wireOp",EDGE,"E12.11.0"),sQuery(id+"F0.wireOp",EDGE,"E12.11.1"),sQuery(id+"F0.wireOp",EDGE,"E12.11.2"),sQuery(id+"F0.wireOp",EDGE,"E12.11.3"),sQuery(id+"F0.wireOp",EDGE,"E12.12.0"),sQuery(id+"F0.wireOp",EDGE,"E12.12.1"),sQuery(id+"F0.wireOp",EDGE,"E12.12.2"),sQuery(id+"F0.wireOp",EDGE,"E12.12.3"),sQuery(id+"F0.wireOp",EDGE,"E12.13.0"),sQuery(id+"F0.wireOp",EDGE,"E12.13.1"),sQuery(id+"F0.wireOp",EDGE,"E12.13.2"),sQuery(id+"F0.wireOp",EDGE,"E12.13.3"),sQuery(id+"F0.wireOp",EDGE,"E12.14.0"),sQuery(id+"F0.wireOp",EDGE,"E12.14.1"),sQuery(id+"F0.wireOp",EDGE,"E12.14.2"),sQuery(id+"F0.wireOp",EDGE,"E12.14.3"),sQuery(id+"F0.wireOp",EDGE,"E12.15.0"),sQuery(id+"F0.wireOp",EDGE,"E12.15.1"),sQuery(id+"F0.wireOp",EDGE,"E12.15.2"),sQuery(id+"F0.wireOp",EDGE,"E12.15.3"),sQuery(id+"F0.wireOp",EDGE,"E12.16.0"),sQuery(id+"F0.wireOp",EDGE,"E12.16.1"),sQuery(id+"F0.wireOp",EDGE,"E12.16.2"),sQuery(id+"F0.wireOp",EDGE,"E12.16.3"),sQuery(id+"F0.wireOp",EDGE,"E12.17.0"),sQuery(id+"F0.wireOp",EDGE,"E12.17.1"),sQuery(id+"F0.wireOp",EDGE,"E12.17.2"),sQuery(id+"F0.wireOp",EDGE,"E12.17.3"),sQuery(id+"F0.wireOp",EDGE,"E12.18.0"),sQuery(id+"F0.wireOp",EDGE,"E12.18.1"),sQuery(id+"F0.wireOp",EDGE,"E12.18.2"),sQuery(id+"F0.wireOp",EDGE,"E12.18.3"),sQuery(id+"F0.wireOp",EDGE,"E12.19.0"),sQuery(id+"F0.wireOp",EDGE,"E12.19.1"),sQuery(id+"F0.wireOp",EDGE,"E12.19.2"),sQuery(id+"F0.wireOp",EDGE,"E12.19.3"),sQuery(id+"F0.wireOp",EDGE,"E12.20.0"),sQuery(id+"F0.wireOp",EDGE,"E12.20.1"),sQuery(id+"F0.wireOp",EDGE,"E12.20.2"),sQuery(id+"F0.wireOp",EDGE,"E12.20.3"),sQuery(id+"F0.wireOp",EDGE,"E12.21.0"),sQuery(id+"F0.wireOp",EDGE,"E12.21.1"),sQuery(id+"F0.wireOp",EDGE,"E12.21.2"),sQuery(id+"F0.wireOp",EDGE,"E12.21.3"),sQuery(id+"F0.wireOp",EDGE,"E12.22.0"),sQuery(id+"F0.wireOp",EDGE,"E12.22.1"),sQuery(id+"F0.wireOp",EDGE,"E12.22.2"),sQuery(id+"F0.wireOp",EDGE,"E12.22.3"),sQuery(id+"F0.wireOp",EDGE,"E12.23.0"),sQuery(id+"F0.wireOp",EDGE,"E12.23.1"),sQuery(id+"F0.wireOp",EDGE,"E12.23.2"),sQuery(id+"F0.wireOp",EDGE,"E12.23.3"),sQuery(id+"F0.wireOp",EDGE,"E12.24.0"),sQuery(id+"F0.wireOp",EDGE,"E12.24.1"),sQuery(id+"F0.wireOp",EDGE,"E12.24.2"),sQuery(id+"F0.wireOp",EDGE,"E12.24.3"),sQuery(id+"F0.wireOp",EDGE,"E12.25.0"),sQuery(id+"F0.wireOp",EDGE,"E12.25.1"),sQuery(id+"F0.wireOp",EDGE,"E12.25.2"),sQuery(id+"F0.wireOp",EDGE,"E12.25.3"),sQuery(id+"F0.wireOp",EDGE,"E12.26.0"),sQuery(id+"F0.wireOp",EDGE,"E12.26.1"),sQuery(id+"F0.wireOp",EDGE,"E12.26.2"),sQuery(id+"F0.wireOp",EDGE,"E12.26.3"),sQuery(id+"F0.wireOp",EDGE,"E12.27.0"),sQuery(id+"F0.wireOp",EDGE,"E12.27.1"),sQuery(id+"F0.wireOp",EDGE,"E12.27.2"),sQuery(id+"F0.wireOp",EDGE,"E12.27.3"),sQuery(id+"F0.wireOp",EDGE,"E12.28.0"),sQuery(id+"F0.wireOp",EDGE,"E12.28.1"),sQuery(id+"F0.wireOp",EDGE,"E12.28.2"),sQuery(id+"F0.wireOp",EDGE,"E12.28.3"),sQuery(id+"F0.wireOp",EDGE,"E12.29.0"),sQuery(id+"F0.wireOp",EDGE,"E12.29.1"),sQuery(id+"F0.wireOp",EDGE,"E12.29.2"),sQuery(id+"F0.wireOp",EDGE,"E12.29.3"),sQuery(id+"F0.wireOp",EDGE,"E12.30.0"),sQuery(id+"F0.wireOp",EDGE,"E12.30.1"),sQuery(id+"F0.wireOp",EDGE,"E12.30.2"),sQuery(id+"F0.wireOp",EDGE,"E12.30.3"),sQuery(id+"F0.wireOp",EDGE,"E12.31.0"),sQuery(id+"F0.wireOp",EDGE,"E12.31.1"),sQuery(id+"F0.wireOp",EDGE,"E12.31.2"),sQuery(id+"F0.wireOp",EDGE,"E12.31.3"),sQuery(id+"F0.wireOp",EDGE,"E12.32.0"),sQuery(id+"F0.wireOp",EDGE,"E12.32.1"),sQuery(id+"F0.wireOp",EDGE,"E12.32.2"),sQuery(id+"F0.wireOp",EDGE,"E12.32.3"),sQuery(id+"F0.wireOp",EDGE,"E12.33.0"),sQuery(id+"F0.wireOp",EDGE,"E12.33.1"),sQuery(id+"F0.wireOp",EDGE,"E12.33.2"),sQuery(id+"F0.wireOp",EDGE,"E12.33.3"),sQuery(id+"F0.wireOp",EDGE,"E12.34.0"),sQuery(id+"F0.wireOp",EDGE,"E12.34.1"),sQuery(id+"F0.wireOp",EDGE,"E12.34.2"),sQuery(id+"F0.wireOp",EDGE,"E12.34.3"),sQuery(id+"F0.wireOp",EDGE,"E12.35.0"),sQuery(id+"F0.wireOp",EDGE,"E12.35.1"),sQuery(id+"F0.wireOp",EDGE,"E12.35.2"),sQuery(id+"F0.wireOp",EDGE,"E12.35.3"),sQuery(id+"F0.wireOp",EDGE,"E12.36.0"),sQuery(id+"F0.wireOp",EDGE,"E12.36.1"),sQuery(id+"F0.wireOp",EDGE,"E12.36.2"),sQuery(id+"F0.wireOp",EDGE,"E12.36.3"),sQuery(id+"F0.wireOp",EDGE,"E12.37.0"),sQuery(id+"F0.wireOp",EDGE,"E12.37.1"),sQuery(id+"F0.wireOp",EDGE,"E12.37.2"),sQuery(id+"F0.wireOp",EDGE,"E12.37.3"),sQuery(id+"F0.wireOp",EDGE,"E12.38.0"),sQuery(id+"F0.wireOp",EDGE,"E12.38.1"),sQuery(id+"F0.wireOp",EDGE,"E12.38.2"),sQuery(id+"F0.wireOp",EDGE,"E12.38.3"),sQuery(id+"F0.wireOp",EDGE,"E12.39.0"),sQuery(id+"F0.wireOp",EDGE,"E12.39.1"),sQuery(id+"F0.wireOp",EDGE,"E12.39.2"),sQuery(id+"F0.wireOp",EDGE,"E12.39.3"),sQuery(id+"F0.wireOp",EDGE,"E12.40.0"),sQuery(id+"F0.wireOp",EDGE,"E12.40.1"),sQuery(id+"F0.wireOp",EDGE,"E12.40.2"),sQuery(id+"F0.wireOp",EDGE,"E12.40.3"),sQuery(id+"F0.wireOp",EDGE,"E12.41.0"),sQuery(id+"F0.wireOp",EDGE,"E12.41.1"),sQuery(id+"F0.wireOp",EDGE,"E12.41.2"),sQuery(id+"F0.wireOp",EDGE,"E12.41.3"),sQuery(id+"F0.wireOp",EDGE,"E13"),sQuery(id+"F0.wireOp",EDGE,"E14.1.0"),sQuery(id+"F0.wireOp",EDGE,"E14.2.0"),sQuery(id+"F0.wireOp",EDGE,"E14.3.0"),sQuery(id+"F0.wireOp",EDGE,"E14.4.0"),sQuery(id+"F0.wireOp",EDGE,"E14.5.0"),sQuery(id+"F0.wireOp",EDGE,"E14.6.0"),sQuery(id+"F0.wireOp",EDGE,"E14.7.0"),sQuery(id+"F0.wireOp",EDGE,"E14.8.0"),sQuery(id+"F0.wireOp",EDGE,"E14.9.0")])],"isStart":true});
            var sketch = newSketch(context, id + "F4", { "sketchPlane" : qUnion([Q0])});
            skCircle(sketch, "E27", {"center": v(0, 0) * mm, "radius": 36.83 * mm});
            skSolve(sketch);
        }
        {
            var Q0;
            Q0=makeQuery(id+"F4.imprint","IMPRINT",FACE,{"disambiguationData":[TD([[makeQuery(id+"F4.imprint","IMPRINT",EDGE,{"derivedFrom":sQuery(id+"F4.wireOp",EDGE,"E27")}),1.0]])]});
            var Q1;
            {var subQ50=sQuery(id+"F0.wireOp",EDGE,"E1");Q1=makeQuery(id+"F4.imprint","IMPRINT",FACE,{"disambiguationData":[TD([[makeQuery(id+"F4.imprint","IMPRINT",EDGE,{"derivedFrom":makeQuery(id+"F1.opExtrude","CAP_EDGE",EDGE,{"disambiguationData":[OSD([subQ50])],"isStart":true})}),1.0]])]});}
            extrude(context, id + "F5", {"entities" : qUnion([Q0, Q1]), "depth" : 1.59 * mm});
        }
    });
